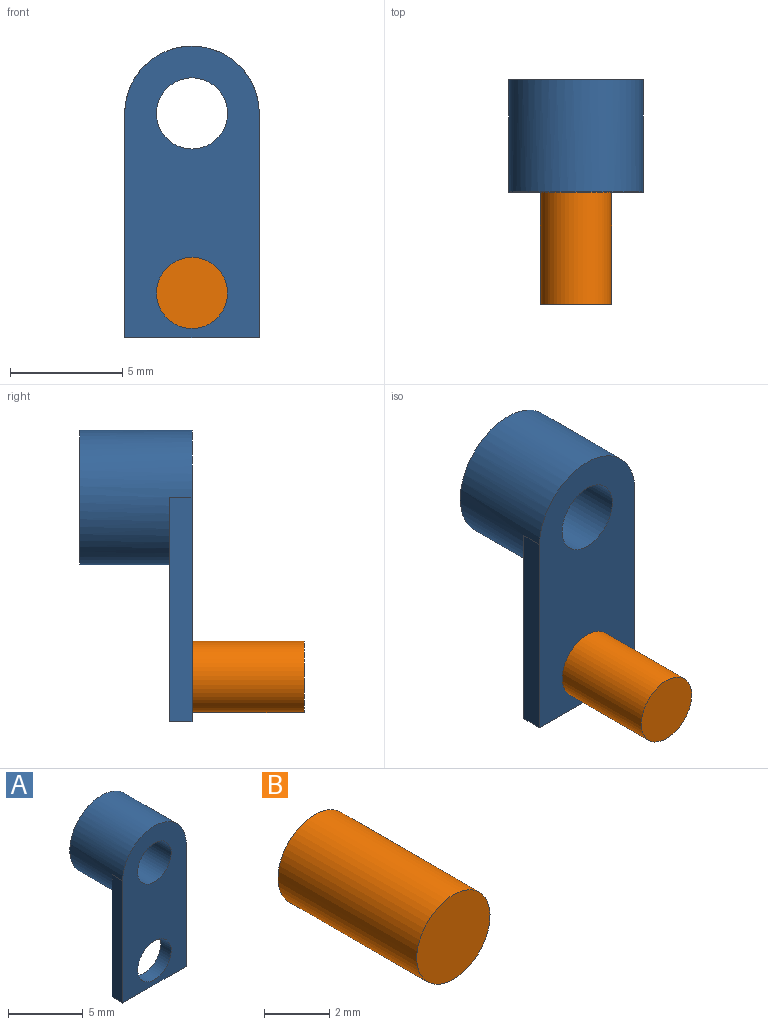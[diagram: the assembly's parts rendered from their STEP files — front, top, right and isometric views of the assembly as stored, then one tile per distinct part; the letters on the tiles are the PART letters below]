
ASSEMBLY  parts=2 mates=1
PART A: 9 faces, bbox 6x5x13 mm
  f0: cylinder r=3mm len=6mm, axis (0,1,0), area 84.8mm2, adj f2,f3,f4,f5,f8
  f1: cylinder r=1.58mm len=5mm, axis (0,1,0), area 49.8mm2, adj f2,f3
  f2: plane 13x6mm, normal (0,-1,0), area 58.4mm2, adj f0,f1,f4,f5,f6,f7
  f3: plane 6x6mm, normal (0,1,0), area 20.4mm2, adj f0,f1
  f4: plane 10x1mm, normal (1,0,0), area 10mm2, adj f0,f2,f7,f8
  f5: plane 10x1mm, normal (-1,0,0), area 10mm2, adj f0,f2,f7,f8
  f6: cylinder r=1.58mm len=3.17mm, axis (0,-1,0), area 10mm2, adj f2,f8
  f7: plane 6x1mm, normal (0,0,-1), area 6mm2, adj f2,f4,f5,f8
  f8: plane 10x6mm, normal (0,1,0), area 38mm2, adj f0,f4,f5,f6,f7
PART B: 3 faces, bbox 3.2x6x3.2 mm
  f0: cylinder r=1.58mm len=6mm, axis (0,1,0), area 59.8mm2, adj f1,f2
  f1: plane 3.17x3.17mm, normal (0,-1,0), area 7.9mm2, adj f0
  f2: plane 3.17x3.17mm, normal (0,1,0), area 7.9mm2, adj f0
PLACE A t=(3.56,4.43,1.06)mm
PLACE B t=(3.56,0.43,-6.94)mm
MATE fastened A.f6 <-> B.f0  axis (0,-1,0) through (3.56,0.43,-6.94)mm
